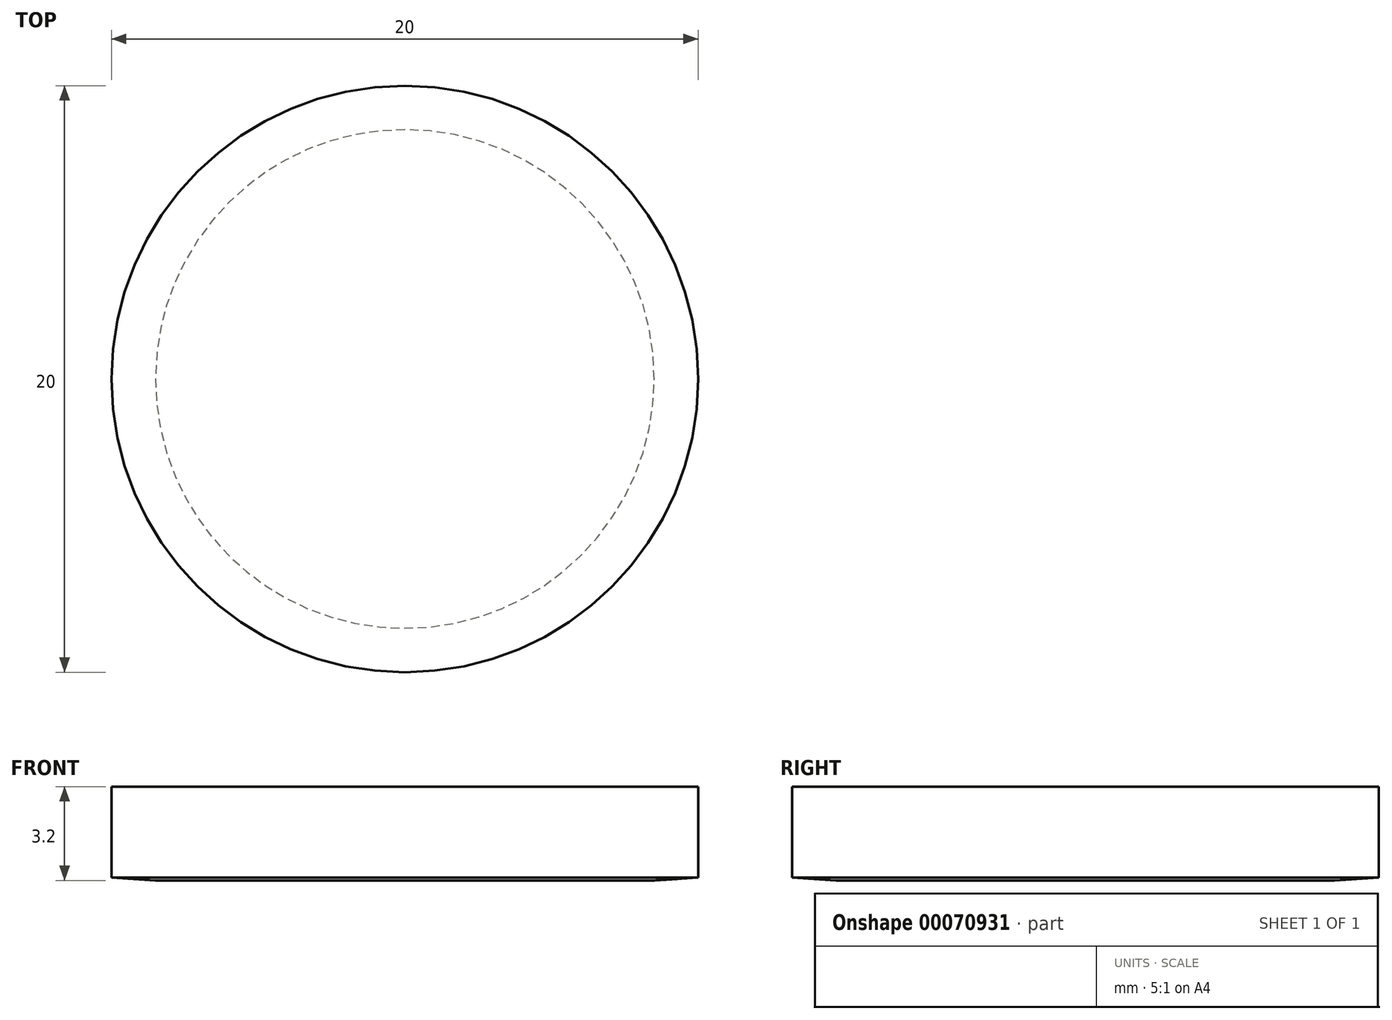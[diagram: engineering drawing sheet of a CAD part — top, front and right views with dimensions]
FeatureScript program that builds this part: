
annotation { "Feature Type Name" : "Feature", "Feature Type Description" : "" }
export const myFeature = defineFeature(function(context is Context, id is Id, definition is map)
    precondition{}
    {
        {
            var Q0;
            Q0=qCreatedBy(makeId("Front.planeOp"),FACE);
            var sketch = newSketch(context, id + "F0", { "sketchPlane" : qUnion([Q0])});
            skLineSegment(sketch, "E0", {"start": v(0, 0) * mm, "end": v(0, 3.2) * mm});
            skLineSegment(sketch, "E1", {"start": v(0, 3.2) * mm, "end": v(10, 3.2) * mm});
            skLineSegment(sketch, "E2", {"start": v(10, 3.2) * mm, "end": v(10, 0.1) * mm});
            skLineSegment(sketch, "E3", {"start": v(10, 0.1) * mm, "end": v(8.5, 0) * mm});
            skLineSegment(sketch, "E4", {"start": v(8.5, 0) * mm, "end": v(0, 0) * mm});
            skLineSegment(sketch, "E5", {"start": v(0, 0) * mm, "end": v(0, -4.78) * mm, "construction": true});
            skSolve(sketch);
        }
        {
            var Q0;
            Q0=makeQuery(id+"F0.imprint","IMPRINT",FACE,{"disambiguationData":[TD([[makeQuery(id+"F0.imprint","IMPRINT",EDGE,{"derivedFrom":sQuery(id+"F0.wireOp",EDGE,"E0")}),-1.0]])]});
            var Q1;
            Q1=sQuery(id+"F0.wireOp",EDGE,"E5");
            revolve(context, id + "F1", {"entities" : qUnion([Q0]), "axis" : qUnion([Q1]), "revolveType" : RevolveType.FULL});
        }
    });
